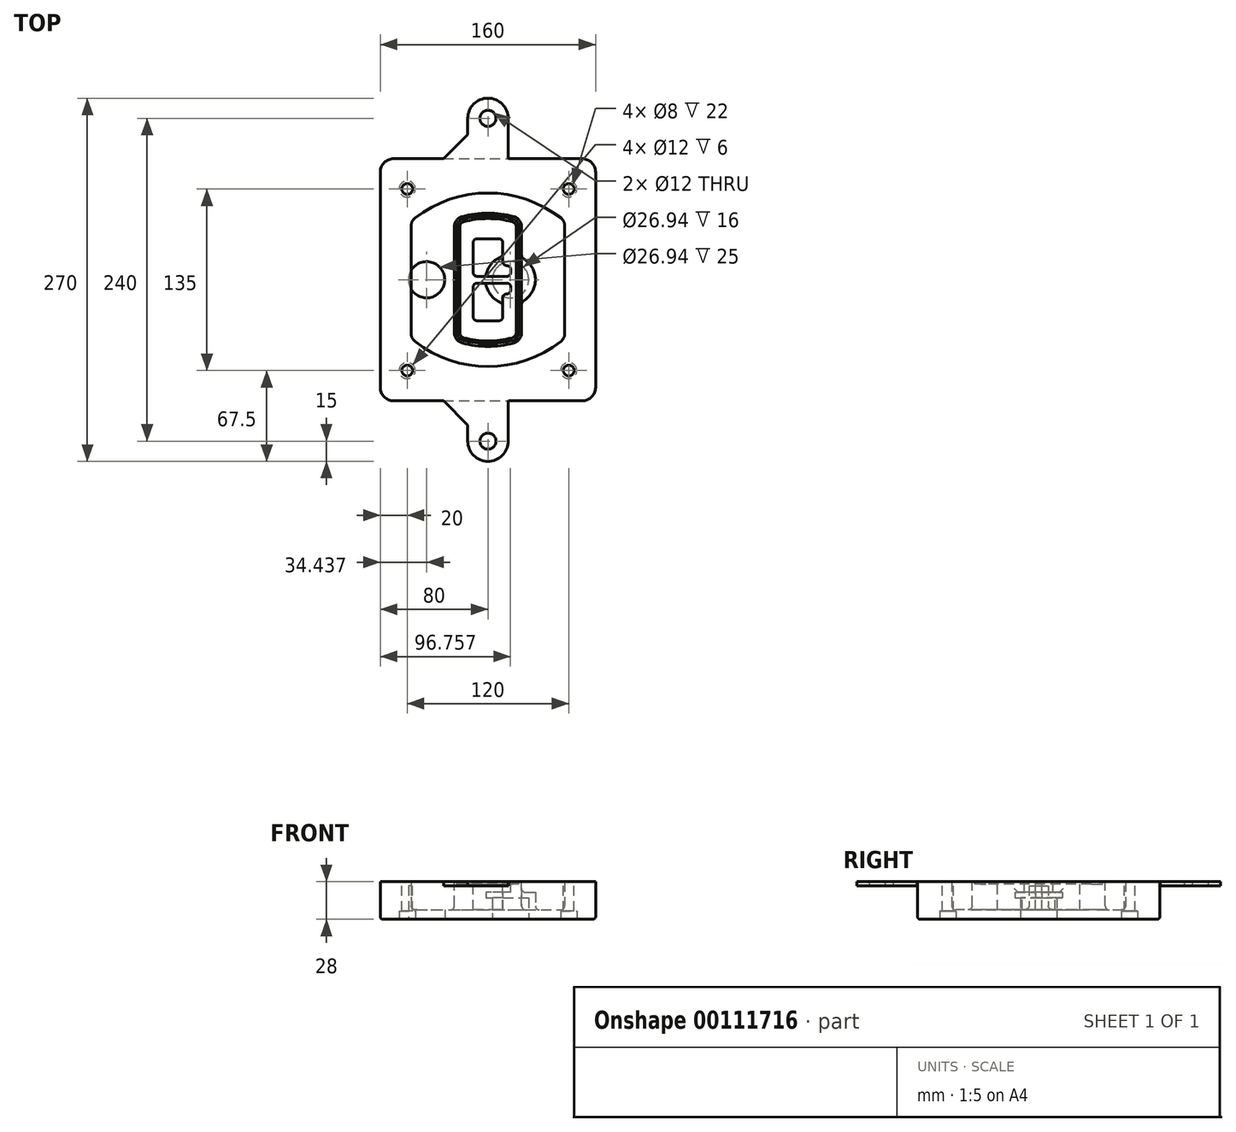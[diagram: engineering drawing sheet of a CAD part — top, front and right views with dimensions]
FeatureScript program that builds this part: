
annotation { "Feature Type Name" : "Feature", "Feature Type Description" : "" }
export const myFeature = defineFeature(function(context is Context, id is Id, definition is map)
    precondition{}
    {
        {
            var Q0;
            Q0=qCreatedBy(makeId("Top.planeOp"),FACE);
            var sketch = newSketch(context, id + "F0", { "sketchPlane" : qUnion([Q0])});
            skPoint(sketch, "E0.rect.middle", {"position": v(0, 0) * mm});
            skLineSegment(sketch, "E1.bottom", {"start": v(-70, -90) * mm, "end": v(70, -90) * mm});
            skLineSegment(sketch, "E1.top", {"start": v(-70, 90) * mm, "end": v(70, 90) * mm});
            skLineSegment(sketch, "E1.left", {"start": v(-80, -80) * mm, "end": v(-80, 80) * mm});
            skLineSegment(sketch, "E1.right", {"start": v(80, -80) * mm, "end": v(80, 80) * mm});
            skLineSegment(sketch, "E2", {"start": v(-80, 90) * mm, "end": v(80, -90) * mm, "construction": true});
            skLineSegment(sketch, "E3", {"start": v(80, 90) * mm, "end": v(-80, -90) * mm, "construction": true});
            skCircle(sketch, "E4", {"center": v(-60, 67.5) * mm, "radius": 4 * mm});
            skCircle(sketch, "E5", {"center": v(60, 67.5) * mm, "radius": 4 * mm});
            skCircle(sketch, "E6", {"center": v(60, -67.5) * mm, "radius": 4 * mm});
            skCircle(sketch, "E7", {"center": v(-60, -67.5) * mm, "radius": 4 * mm});
            skLineSegment(sketch, "E8", {"start": v(-60, 67.5) * mm, "end": v(60, 67.5) * mm, "construction": true});
            skLineSegment(sketch, "E9", {"start": v(60, 67.5) * mm, "end": v(60, -67.5) * mm, "construction": true});
            skLineSegment(sketch, "E10", {"start": v(60, -67.5) * mm, "end": v(-60, -67.5) * mm, "construction": true});
            skLineSegment(sketch, "E11", {"start": v(-60, -67.5) * mm, "end": v(-60, 67.5) * mm, "construction": true});
            skLineSegment(sketch, "E12", {"start": v(-60, 40.3) * mm, "end": v(-60, -40.3) * mm});
            skLineSegment(sketch, "E13", {"start": v(60, 40.3) * mm, "end": v(60, -40.3) * mm});
            skArc(sketch, "E14", {"start": v(56.15, 48.18) * mm, "mid": v(0, 67.5) * mm, "end": v(-56.15, 48.18) * mm});
            skArc(sketch, "E15", {"start": v(-56.15, -48.18) * mm, "mid": v(0, -67.5) * mm, "end": v(56.15, -48.18) * mm});
            skLineSegment(sketch, "E16", {"start": v(-60, 0) * mm, "end": v(60, 0) * mm, "construction": true});
            skPoint(sketch, "E17.visualSharp", {"position": v(-60, -45) * mm});
            skArc(sketch, "E17.filletArc", {"start": v(-60, -40.3) * mm, "mid": v(-58.99, -44.68) * mm, "end": v(-56.15, -48.18) * mm});
            skPoint(sketch, "E18.visualSharp", {"position": v(-60, 45) * mm});
            skArc(sketch, "E18.filletArc", {"start": v(-56.15, 48.18) * mm, "mid": v(-58.99, 44.68) * mm, "end": v(-60, 40.3) * mm});
            skPoint(sketch, "E19.visualSharp", {"position": v(60, 45) * mm});
            skArc(sketch, "E19.filletArc", {"start": v(60, 40.3) * mm, "mid": v(58.99, 44.68) * mm, "end": v(56.15, 48.18) * mm});
            skPoint(sketch, "E20.visualSharp", {"position": v(60, -45) * mm});
            skArc(sketch, "E20.filletArc", {"start": v(56.15, -48.18) * mm, "mid": v(58.99, -44.68) * mm, "end": v(60, -40.3) * mm});
            skPoint(sketch, "E21.visualSharp", {"position": v(-80, 90) * mm});
            skArc(sketch, "E21.filletArc", {"start": v(-70, 90) * mm, "mid": v(-77.07, 87.07) * mm, "end": v(-80, 80) * mm});
            skPoint(sketch, "E22.visualSharp", {"position": v(80, 90) * mm});
            skArc(sketch, "E22.filletArc", {"start": v(80, 80) * mm, "mid": v(77.07, 87.07) * mm, "end": v(70, 90) * mm});
            skPoint(sketch, "E23.visualSharp", {"position": v(80, -90) * mm});
            skArc(sketch, "E23.filletArc", {"start": v(70, -90) * mm, "mid": v(77.07, -87.07) * mm, "end": v(80, -80) * mm});
            skPoint(sketch, "E24.visualSharp", {"position": v(-80, -90) * mm});
            skArc(sketch, "E24.filletArc", {"start": v(-80, -80) * mm, "mid": v(-77.07, -87.07) * mm, "end": v(-70, -90) * mm});
            skArc(sketch, "E25.0", {"start": v(57, 40.3) * mm, "mid": v(56.3, 43.36) * mm, "end": v(54.3, 45.81) * mm});
            skLineSegment(sketch, "E25.1", {"start": v(57, 40.3) * mm, "end": v(57, -40.3) * mm});
            skArc(sketch, "E25.2", {"start": v(54.3, -45.81) * mm, "mid": v(56.3, -43.36) * mm, "end": v(57, -40.3) * mm});
            skArc(sketch, "E25.3", {"start": v(-54.3, -45.81) * mm, "mid": v(0, -64.5) * mm, "end": v(54.3, -45.81) * mm});
            skArc(sketch, "E25.4", {"start": v(-57, -40.3) * mm, "mid": v(-56.3, -43.36) * mm, "end": v(-54.3, -45.81) * mm});
            skArc(sketch, "E25.5", {"start": v(54.3, 45.81) * mm, "mid": v(0, 64.5) * mm, "end": v(-54.3, 45.81) * mm});
            skLineSegment(sketch, "E25.6", {"start": v(-57, 40.3) * mm, "end": v(-57, -40.3) * mm});
            skArc(sketch, "E25.7", {"start": v(-54.3, 45.81) * mm, "mid": v(-56.3, 43.36) * mm, "end": v(-57, 40.3) * mm});
            skArc(sketch, "E26.0", {"start": v(-58.62, 51.33) * mm, "mid": v(-62.58, 46.43) * mm, "end": v(-64, 40.3) * mm});
            skArc(sketch, "E26.1", {"start": v(58.62, 51.33) * mm, "mid": v(0, 71.5) * mm, "end": v(-58.62, 51.33) * mm});
            skArc(sketch, "E26.2", {"start": v(64, 40.3) * mm, "mid": v(62.58, 46.43) * mm, "end": v(58.62, 51.33) * mm});
            skLineSegment(sketch, "E26.3", {"start": v(64, 40.3) * mm, "end": v(64, -40.3) * mm});
            skArc(sketch, "E26.4", {"start": v(58.62, -51.33) * mm, "mid": v(62.58, -46.43) * mm, "end": v(64, -40.3) * mm});
            skLineSegment(sketch, "E26.5", {"start": v(-64, 40.3) * mm, "end": v(-64, -40.3) * mm});
            skArc(sketch, "E26.6", {"start": v(-58.62, -51.33) * mm, "mid": v(0, -71.5) * mm, "end": v(58.62, -51.33) * mm});
            skArc(sketch, "E26.7", {"start": v(-64, -40.3) * mm, "mid": v(-62.58, -46.43) * mm, "end": v(-58.62, -51.33) * mm});
            skSolve(sketch);
        }
        {
            var Q0;
            Q0=makeQuery(id+"F0.imprint","IMPRINT",FACE,{"disambiguationData":[TD([[makeQuery(id+"F0.imprint","IMPRINT",EDGE,{"derivedFrom":sQuery(id+"F0.wireOp",EDGE,"E1.bottom")}),1.0]])]});
            var Q1;
            Q1=makeQuery(id+"F0.imprint","IMPRINT",FACE,{"disambiguationData":[TD([[makeQuery(id+"F0.imprint","IMPRINT",EDGE,{"derivedFrom":sQuery(id+"F0.wireOp",EDGE,"E12")}),1.0]])]});
            var Q2;
            Q2=makeQuery(id+"F0.imprint","IMPRINT",FACE,{"disambiguationData":[TD([[makeQuery(id+"F0.imprint","IMPRINT",EDGE,{"derivedFrom":sQuery(id+"F0.wireOp",EDGE,"E25.0")}),1.0]])]});
            var Q3;
            Q3=makeQuery(id+"F0.imprint","IMPRINT",FACE,{"disambiguationData":[TD([[makeQuery(id+"F0.imprint","IMPRINT",EDGE,{"derivedFrom":sQuery(id+"F0.wireOp",EDGE,"E12")}),-1.0]])]});
            extrude(context, id + "F1", {"entities" : qUnion([Q0, Q1, Q2, Q3]), "oppositeDirection" : true, "depth" : 25 * mm});
        }
        {
            var Q0;
            Q0=makeQuery(id+"F0.imprint","IMPRINT",FACE,{"disambiguationData":[TD([[makeQuery(id+"F0.imprint","IMPRINT",EDGE,{"derivedFrom":sQuery(id+"F0.wireOp",EDGE,"E12")}),1.0]])]});
            extrude(context, id + "F2", {"entities" : qUnion([Q0]), "operationType" : NewBodyOperationType.ADD, "depth" : 3 * mm});
        }
        {
            var Q0;
            Q0=makeQuery(id+"F0.imprint","IMPRINT",FACE,{"disambiguationData":[TD([[makeQuery(id+"F0.imprint","IMPRINT",EDGE,{"derivedFrom":sQuery(id+"F0.wireOp",EDGE,"E25.0")}),1.0]])]});
            extrude(context, id + "F3", {"entities" : qUnion([Q0]), "operationType" : NewBodyOperationType.REMOVE, "oppositeDirection" : true, "depth" : 18 * mm});
        }
        {
            var Q0;
            Q0=makeQuery(id+"F2.opExtrude","CAP_FACE",FACE,{"disambiguationData":[OSD([sQuery(id+"F0.wireOp",EDGE,"E12"),sQuery(id+"F0.wireOp",EDGE,"E13"),sQuery(id+"F0.wireOp",EDGE,"E14"),sQuery(id+"F0.wireOp",EDGE,"E15"),sQuery(id+"F0.wireOp",EDGE,"E17.filletArc"),sQuery(id+"F0.wireOp",EDGE,"E18.filletArc"),sQuery(id+"F0.wireOp",EDGE,"E19.filletArc"),sQuery(id+"F0.wireOp",EDGE,"E20.filletArc"),sQuery(id+"F0.wireOp",EDGE,"E25.0"),sQuery(id+"F0.wireOp",EDGE,"E25.1"),sQuery(id+"F0.wireOp",EDGE,"E25.2"),sQuery(id+"F0.wireOp",EDGE,"E25.3"),sQuery(id+"F0.wireOp",EDGE,"E25.4"),sQuery(id+"F0.wireOp",EDGE,"E25.5"),sQuery(id+"F0.wireOp",EDGE,"E25.6"),sQuery(id+"F0.wireOp",EDGE,"E25.7")])],"isStart":false});
            var sketch = newSketch(context, id + "F4", { "sketchPlane" : qUnion([Q0])});
            skArc(sketch, "E27.0", {"start": v(-19.08, -46.97) * mm, "mid": v(0, -49.5) * mm, "end": v(19.08, -46.97) * mm});
            skArc(sketch, "E28.0", {"start": v(19.08, 46.97) * mm, "mid": v(0, 49.5) * mm, "end": v(-19.08, 46.97) * mm});
            skLineSegment(sketch, "E29", {"start": v(-25, 39.25) * mm, "end": v(-25, -39.25) * mm});
            skLineSegment(sketch, "E30", {"start": v(25, 39.25) * mm, "end": v(25, -39.25) * mm});
            skLineSegment(sketch, "E31", {"start": v(-25, 45.1) * mm, "end": v(25, 45.1) * mm, "construction": true});
            skLineSegment(sketch, "E32", {"start": v(-25, -45.1) * mm, "end": v(25, -45.1) * mm, "construction": true});
            skPoint(sketch, "E33.visualSharp", {"position": v(-25, 45.1) * mm});
            skArc(sketch, "E33.filletArc", {"start": v(-19.08, 46.97) * mm, "mid": v(-23.35, 44.11) * mm, "end": v(-25, 39.25) * mm});
            skPoint(sketch, "E34.visualSharp", {"position": v(25, 45.1) * mm});
            skArc(sketch, "E34.filletArc", {"start": v(25, 39.25) * mm, "mid": v(23.35, 44.11) * mm, "end": v(19.08, 46.97) * mm});
            skPoint(sketch, "E35.visualSharp", {"position": v(25, -45.1) * mm});
            skArc(sketch, "E35.filletArc", {"start": v(19.08, -46.97) * mm, "mid": v(23.35, -44.11) * mm, "end": v(25, -39.25) * mm});
            skPoint(sketch, "E36.visualSharp", {"position": v(-25, -45.1) * mm});
            skArc(sketch, "E36.filletArc", {"start": v(-25, -39.25) * mm, "mid": v(-23.35, -44.11) * mm, "end": v(-19.08, -46.97) * mm});
            skArc(sketch, "E37.0", {"start": v(54.3, 45.81) * mm, "mid": v(0, 64.5) * mm, "end": v(-54.3, 45.81) * mm});
            skArc(sketch, "E37.1", {"start": v(-54.3, 45.81) * mm, "mid": v(-56.3, 43.36) * mm, "end": v(-57, 40.3) * mm});
            skLineSegment(sketch, "E37.2", {"start": v(-57, 40.3) * mm, "end": v(-57, -40.3) * mm});
            skArc(sketch, "E37.3", {"start": v(-57, -40.3) * mm, "mid": v(-56.3, -43.36) * mm, "end": v(-54.3, -45.81) * mm});
            skArc(sketch, "E37.4", {"start": v(-54.3, -45.81) * mm, "mid": v(0, -64.5) * mm, "end": v(54.3, -45.81) * mm});
            skArc(sketch, "E37.5", {"start": v(54.3, -45.81) * mm, "mid": v(56.3, -43.36) * mm, "end": v(57, -40.3) * mm});
            skLineSegment(sketch, "E37.6", {"start": v(57, 40.3) * mm, "end": v(57, -40.3) * mm});
            skArc(sketch, "E37.7", {"start": v(57, 40.3) * mm, "mid": v(56.3, 43.36) * mm, "end": v(54.3, 45.81) * mm});
            skLineSegment(sketch, "E38.0", {"start": v(23, 39.25) * mm, "end": v(23, -39.25) * mm});
            skArc(sketch, "E38.1", {"start": v(18.56, -45.04) * mm, "mid": v(21.76, -42.9) * mm, "end": v(23, -39.25) * mm});
            skArc(sketch, "E38.2", {"start": v(-18.56, -45.04) * mm, "mid": v(0, -47.5) * mm, "end": v(18.56, -45.04) * mm});
            skArc(sketch, "E38.3", {"start": v(-23, -39.25) * mm, "mid": v(-21.76, -42.9) * mm, "end": v(-18.56, -45.04) * mm});
            skLineSegment(sketch, "E38.4", {"start": v(-23, 39.25) * mm, "end": v(-23, -39.25) * mm});
            skArc(sketch, "E38.5", {"start": v(23, 39.25) * mm, "mid": v(21.76, 42.9) * mm, "end": v(18.56, 45.04) * mm});
            skArc(sketch, "E38.6", {"start": v(-18.56, 45.04) * mm, "mid": v(-21.76, 42.9) * mm, "end": v(-23, 39.25) * mm});
            skArc(sketch, "E38.7", {"start": v(18.56, 45.04) * mm, "mid": v(0, 47.5) * mm, "end": v(-18.56, 45.04) * mm});
            skArc(sketch, "E39.0", {"start": v(21, 39.25) * mm, "mid": v(20.18, 41.68) * mm, "end": v(18.04, 43.1) * mm});
            skLineSegment(sketch, "E39.1", {"start": v(21, 39.25) * mm, "end": v(21, -39.25) * mm});
            skArc(sketch, "E39.2", {"start": v(18.04, -43.1) * mm, "mid": v(20.18, -41.68) * mm, "end": v(21, -39.25) * mm});
            skArc(sketch, "E39.3", {"start": v(-18.04, -43.1) * mm, "mid": v(0, -45.5) * mm, "end": v(18.04, -43.1) * mm});
            skArc(sketch, "E39.4", {"start": v(-21, -39.25) * mm, "mid": v(-20.18, -41.68) * mm, "end": v(-18.04, -43.1) * mm});
            skArc(sketch, "E39.5", {"start": v(18.04, 43.1) * mm, "mid": v(0, 45.5) * mm, "end": v(-18.04, 43.1) * mm});
            skLineSegment(sketch, "E39.6", {"start": v(-21, 39.25) * mm, "end": v(-21, -39.25) * mm});
            skArc(sketch, "E39.7", {"start": v(-18.04, 43.1) * mm, "mid": v(-20.18, 41.68) * mm, "end": v(-21, 39.25) * mm});
            skLineSegment(sketch, "E40", {"start": v(-25, 0) * mm, "end": v(25, 0) * mm, "construction": true});
            skLineSegment(sketch, "E41", {"start": v(-11, 5.5) * mm, "end": v(-11, 27.5) * mm});
            skLineSegment(sketch, "E42", {"start": v(-8, 30.5) * mm, "end": v(8, 30.5) * mm});
            skLineSegment(sketch, "E43", {"start": v(11, 27.5) * mm, "end": v(11, 13.5) * mm});
            skLineSegment(sketch, "E44", {"start": v(14, 10.5) * mm, "end": v(14, 10.5) * mm});
            skLineSegment(sketch, "E45", {"start": v(17, 7.5) * mm, "end": v(17, 5.5) * mm});
            skLineSegment(sketch, "E46", {"start": v(14, 2.5) * mm, "end": v(-8, 2.5) * mm});
            skPoint(sketch, "E47.visualSharp", {"position": v(-11, 30.5) * mm});
            skArc(sketch, "E47.filletArc", {"start": v(-8, 30.5) * mm, "mid": v(-10.12, 29.62) * mm, "end": v(-11, 27.5) * mm});
            skPoint(sketch, "E48.visualSharp", {"position": v(11, 30.5) * mm});
            skArc(sketch, "E48.filletArc", {"start": v(11, 27.5) * mm, "mid": v(10.12, 29.62) * mm, "end": v(8, 30.5) * mm});
            skPoint(sketch, "E49.visualSharp", {"position": v(11, 10.5) * mm});
            skArc(sketch, "E49.filletArc", {"start": v(11, 13.5) * mm, "mid": v(11.88, 11.38) * mm, "end": v(14, 10.5) * mm});
            skPoint(sketch, "E50.visualSharp", {"position": v(17, 10.5) * mm});
            skArc(sketch, "E50.filletArc", {"start": v(17, 7.5) * mm, "mid": v(16.12, 9.62) * mm, "end": v(14, 10.5) * mm});
            skPoint(sketch, "E51.visualSharp", {"position": v(17, 2.5) * mm});
            skArc(sketch, "E51.filletArc", {"start": v(14, 2.5) * mm, "mid": v(16.12, 3.38) * mm, "end": v(17, 5.5) * mm});
            skPoint(sketch, "E52.visualSharp", {"position": v(-11, 2.5) * mm});
            skArc(sketch, "E52.filletArc", {"start": v(-11, 5.5) * mm, "mid": v(-10.12, 3.38) * mm, "end": v(-8, 2.5) * mm});
            skLineSegment(sketch, "E53.0.MirrorCS", {"start": v(14, -2.5) * mm, "end": v(-8, -2.5) * mm});
            skArc(sketch, "E54.0.MirrorCS", {"start": v(-11, -5.5) * mm, "mid": v(-10.12, -3.38) * mm, "end": v(-8, -2.5) * mm});
            skLineSegment(sketch, "E55.0.MirrorCS", {"start": v(-11, -5.5) * mm, "end": v(-11, -27.5) * mm});
            skArc(sketch, "E56.0.MirrorCS", {"start": v(-8, -30.5) * mm, "mid": v(-10.12, -29.62) * mm, "end": v(-11, -27.5) * mm});
            skLineSegment(sketch, "E57.0.MirrorCS", {"start": v(-8, -30.5) * mm, "end": v(8, -30.5) * mm});
            skArc(sketch, "E58.0.MirrorCS", {"start": v(11, -27.5) * mm, "mid": v(10.12, -29.62) * mm, "end": v(8, -30.5) * mm});
            skLineSegment(sketch, "E59.0.MirrorCS", {"start": v(11, -27.5) * mm, "end": v(11, -13.5) * mm});
            skArc(sketch, "E60.0.MirrorCS", {"start": v(11, -13.5) * mm, "mid": v(11.88, -11.38) * mm, "end": v(14, -10.5) * mm});
            skArc(sketch, "E61.0.MirrorCS", {"start": v(17, -7.5) * mm, "mid": v(16.12, -9.62) * mm, "end": v(14, -10.5) * mm});
            skLineSegment(sketch, "E62.0.MirrorCS", {"start": v(17, -7.5) * mm, "end": v(17, -5.5) * mm});
            skArc(sketch, "E63.0.MirrorCS", {"start": v(14, -2.5) * mm, "mid": v(16.12, -3.38) * mm, "end": v(17, -5.5) * mm});
            skSolve(sketch);
        }
        {
            var Q0;
            Q0=makeQuery(id+"F4.imprint","IMPRINT",FACE,{"disambiguationData":[TD([[makeQuery(id+"F4.imprint","IMPRINT",EDGE,{"derivedFrom":sQuery(id+"F4.wireOp",EDGE,"E27.0")}),1.0]])]});
            var Q1;
            Q1=makeQuery(id+"F4.imprint","IMPRINT",FACE,{"disambiguationData":[TD([[makeQuery(id+"F4.imprint","IMPRINT",EDGE,{"derivedFrom":sQuery(id+"F4.wireOp",EDGE,"E38.0")}),-1.0]])]});
            var Q2;
            Q2=makeQuery(id+"F4.imprint","IMPRINT",FACE,{"disambiguationData":[TD([[makeQuery(id+"F4.imprint","IMPRINT",EDGE,{"derivedFrom":sQuery(id+"F4.wireOp",EDGE,"E39.0")}),1.0]])]});
            extrude(context, id + "F5", {"entities" : qUnion([Q0, Q1, Q2]), "operationType" : NewBodyOperationType.ADD, "endBound" : BoundingType.UP_TO_NEXT, "oppositeDirection" : true, "depth" : 25 * mm});
        }
        {
            var Q0;
            Q0=makeQuery(id+"F4.imprint","IMPRINT",FACE,{"disambiguationData":[TD([[makeQuery(id+"F4.imprint","IMPRINT",EDGE,{"derivedFrom":sQuery(id+"F4.wireOp",EDGE,"E38.0")}),-1.0]])]});
            extrude(context, id + "F6", {"entities" : qUnion([Q0]), "operationType" : NewBodyOperationType.REMOVE, "oppositeDirection" : true, "depth" : 2 * mm});
        }
        {
            var Q0;
            Q0=makeQuery(id+"F1.opExtrude","CAP_FACE",FACE,{"disambiguationData":[OSD([sQuery(id+"F0.wireOp",EDGE,"E1.bottom"),sQuery(id+"F0.wireOp",EDGE,"E1.top"),sQuery(id+"F0.wireOp",EDGE,"E1.left"),sQuery(id+"F0.wireOp",EDGE,"E1.right"),sQuery(id+"F0.wireOp",EDGE,"E4"),sQuery(id+"F0.wireOp",EDGE,"E5"),sQuery(id+"F0.wireOp",EDGE,"E6"),sQuery(id+"F0.wireOp",EDGE,"E7"),sQuery(id+"F0.wireOp",EDGE,"E21.filletArc"),sQuery(id+"F0.wireOp",EDGE,"E22.filletArc"),sQuery(id+"F0.wireOp",EDGE,"E23.filletArc"),sQuery(id+"F0.wireOp",EDGE,"E24.filletArc")])],"isStart":false});
            var sketch = newSketch(context, id + "F7", { "sketchPlane" : qUnion([Q0])});
            skCircle(sketch, "E64", {"center": v(16.76, 0) * mm, "radius": 13.47 * mm});
            skCircle(sketch, "E65", {"center": v(-45.56, 0) * mm, "radius": 13.47 * mm});
            skLineSegment(sketch, "E66", {"start": v(80, 0) * mm, "end": v(-80, 0) * mm});
            skCircle(sketch, "E67", {"center": v(16.76, 0) * mm, "radius": 18.47 * mm});
            skCircle(sketch, "E68", {"center": v(60, -67.5) * mm, "radius": 6 * mm});
            skCircle(sketch, "E69", {"center": v(-60, -67.5) * mm, "radius": 6 * mm});
            skCircle(sketch, "E70", {"center": v(-60, 67.5) * mm, "radius": 6 * mm});
            skCircle(sketch, "E71", {"center": v(60, 67.5) * mm, "radius": 6 * mm});
            skSolve(sketch);
        }
        {
            var Q0;
            {var subQ1=sQuery(id+"F7.wireOp",EDGE,"E66");var subQ4=sQuery(id+"F7.wireOp",EDGE,"E64");var subQ6=makeQuery(id+"F7.imprint","INTERSECT",VERTEX,{"disambiguationData":[OD(0.0)],"derivedFrom":[subQ4,subQ1]});Q0=makeQuery(id+"F7.imprint","IMPRINT",FACE,{"disambiguationData":[TD([[makeQuery(id+"F7.imprint","IMPRINT",EDGE,{"disambiguationData":[TD([[subQ6,-1.0]])],"derivedFrom":subQ4}),-1.0]])]});}
            var Q1;
            {var subQ0=sQuery(id+"F7.wireOp",EDGE,"E66");var subQ1=sQuery(id+"F7.wireOp",EDGE,"E64");var subQ3=makeQuery(id+"F7.imprint","INTERSECT",VERTEX,{"disambiguationData":[OD(0.0)],"derivedFrom":[subQ1,subQ0]});Q1=makeQuery(id+"F7.imprint","IMPRINT",FACE,{"disambiguationData":[TD([[makeQuery(id+"F7.imprint","IMPRINT",EDGE,{"disambiguationData":[TD([[subQ3,-1.0]])],"derivedFrom":subQ1}),1.0]])]});}
            var Q2;
            {var subQ0=sQuery(id+"F7.wireOp",EDGE,"E66");var subQ1=sQuery(id+"F7.wireOp",EDGE,"E64");var subQ3=makeQuery(id+"F7.imprint","INTERSECT",VERTEX,{"disambiguationData":[OD(0.0)],"derivedFrom":[subQ1,subQ0]});Q2=makeQuery(id+"F7.imprint","IMPRINT",FACE,{"disambiguationData":[TD([[makeQuery(id+"F7.imprint","IMPRINT",EDGE,{"disambiguationData":[TD([[subQ3,1.0]])],"derivedFrom":subQ1}),1.0]])]});}
            var Q3;
            {var subQ1=sQuery(id+"F7.wireOp",EDGE,"E66");var subQ4=sQuery(id+"F7.wireOp",EDGE,"E64");var subQ6=makeQuery(id+"F7.imprint","INTERSECT",VERTEX,{"disambiguationData":[OD(0.0)],"derivedFrom":[subQ4,subQ1]});Q3=makeQuery(id+"F7.imprint","IMPRINT",FACE,{"disambiguationData":[TD([[makeQuery(id+"F7.imprint","IMPRINT",EDGE,{"disambiguationData":[TD([[subQ6,1.0]])],"derivedFrom":subQ4}),-1.0]])]});}
            extrude(context, id + "F8", {"entities" : qUnion([Q0, Q1, Q2, Q3]), "operationType" : NewBodyOperationType.ADD, "oppositeDirection" : true, "depth" : 20 * mm});
        }
        {
            var Q0;
            {var subQ0=sQuery(id+"F7.wireOp",EDGE,"E66");var subQ1=sQuery(id+"F7.wireOp",EDGE,"E64");var subQ3=makeQuery(id+"F7.imprint","INTERSECT",VERTEX,{"disambiguationData":[OD(0.0)],"derivedFrom":[subQ1,subQ0]});Q0=makeQuery(id+"F7.imprint","IMPRINT",FACE,{"disambiguationData":[TD([[makeQuery(id+"F7.imprint","IMPRINT",EDGE,{"disambiguationData":[TD([[subQ3,-1.0]])],"derivedFrom":subQ1}),1.0]])]});}
            var Q1;
            {var subQ0=sQuery(id+"F7.wireOp",EDGE,"E66");var subQ1=sQuery(id+"F7.wireOp",EDGE,"E64");var subQ3=makeQuery(id+"F7.imprint","INTERSECT",VERTEX,{"disambiguationData":[OD(0.0)],"derivedFrom":[subQ1,subQ0]});Q1=makeQuery(id+"F7.imprint","IMPRINT",FACE,{"disambiguationData":[TD([[makeQuery(id+"F7.imprint","IMPRINT",EDGE,{"disambiguationData":[TD([[subQ3,1.0]])],"derivedFrom":subQ1}),1.0]])]});}
            extrude(context, id + "F9", {"entities" : qUnion([Q0, Q1]), "operationType" : NewBodyOperationType.REMOVE, "oppositeDirection" : true, "depth" : 16 * mm});
        }
        {
            var Q0;
            {var subQ0=sQuery(id+"F7.wireOp",EDGE,"E66");var subQ1=sQuery(id+"F7.wireOp",EDGE,"E65");var subQ3=makeQuery(id+"F7.imprint","INTERSECT",VERTEX,{"disambiguationData":[OD(0.0)],"derivedFrom":[subQ1,subQ0]});Q0=makeQuery(id+"F7.imprint","IMPRINT",FACE,{"disambiguationData":[TD([[makeQuery(id+"F7.imprint","IMPRINT",EDGE,{"disambiguationData":[TD([[subQ3,-1.0]])],"derivedFrom":subQ1}),1.0]])]});}
            var Q1;
            {var subQ0=sQuery(id+"F7.wireOp",EDGE,"E66");var subQ1=sQuery(id+"F7.wireOp",EDGE,"E65");var subQ3=makeQuery(id+"F7.imprint","INTERSECT",VERTEX,{"disambiguationData":[OD(0.0)],"derivedFrom":[subQ1,subQ0]});Q1=makeQuery(id+"F7.imprint","IMPRINT",FACE,{"disambiguationData":[TD([[makeQuery(id+"F7.imprint","IMPRINT",EDGE,{"disambiguationData":[TD([[subQ3,1.0]])],"derivedFrom":subQ1}),1.0]])]});}
            extrude(context, id + "F10", {"entities" : qUnion([Q0, Q1]), "operationType" : NewBodyOperationType.REMOVE, "oppositeDirection" : true, "depth" : 25 * mm});
        }
        {
            var Q0;
            Q0=makeQuery(id+"F7.imprint","IMPRINT",FACE,{"disambiguationData":[TD([[makeQuery(id+"F7.imprint","IMPRINT",EDGE,{"derivedFrom":sQuery(id+"F7.wireOp",EDGE,"E68")}),1.0]])]});
            var Q1;
            Q1=makeQuery(id+"F7.imprint","IMPRINT",FACE,{"disambiguationData":[TD([[makeQuery(id+"F7.imprint","IMPRINT",EDGE,{"derivedFrom":makeQuery(id+"F1.opExtrude","CAP_EDGE",EDGE,{"disambiguationData":[OSD([sQuery(id+"F0.wireOp",EDGE,"E5")])],"isStart":false})}),-1.0]])]});
            var Q2;
            Q2=makeQuery(id+"F7.imprint","IMPRINT",FACE,{"disambiguationData":[TD([[makeQuery(id+"F7.imprint","IMPRINT",EDGE,{"derivedFrom":sQuery(id+"F7.wireOp",EDGE,"E69")}),1.0]])]});
            var Q3;
            Q3=makeQuery(id+"F7.imprint","IMPRINT",FACE,{"disambiguationData":[TD([[makeQuery(id+"F7.imprint","IMPRINT",EDGE,{"derivedFrom":makeQuery(id+"F1.opExtrude","CAP_EDGE",EDGE,{"disambiguationData":[OSD([sQuery(id+"F0.wireOp",EDGE,"E4")])],"isStart":false})}),-1.0]])]});
            var Q4;
            Q4=makeQuery(id+"F7.imprint","IMPRINT",FACE,{"disambiguationData":[TD([[makeQuery(id+"F7.imprint","IMPRINT",EDGE,{"derivedFrom":sQuery(id+"F7.wireOp",EDGE,"E70")}),1.0]])]});
            var Q5;
            Q5=makeQuery(id+"F7.imprint","IMPRINT",FACE,{"disambiguationData":[TD([[makeQuery(id+"F7.imprint","IMPRINT",EDGE,{"derivedFrom":makeQuery(id+"F1.opExtrude","CAP_EDGE",EDGE,{"disambiguationData":[OSD([sQuery(id+"F0.wireOp",EDGE,"E7")])],"isStart":false})}),-1.0]])]});
            var Q6;
            Q6=makeQuery(id+"F7.imprint","IMPRINT",FACE,{"disambiguationData":[TD([[makeQuery(id+"F7.imprint","IMPRINT",EDGE,{"derivedFrom":sQuery(id+"F7.wireOp",EDGE,"E71")}),1.0]])]});
            var Q7;
            Q7=makeQuery(id+"F7.imprint","IMPRINT",FACE,{"disambiguationData":[TD([[makeQuery(id+"F7.imprint","IMPRINT",EDGE,{"derivedFrom":makeQuery(id+"F1.opExtrude","CAP_EDGE",EDGE,{"disambiguationData":[OSD([sQuery(id+"F0.wireOp",EDGE,"E6")])],"isStart":false})}),-1.0]])]});
            extrude(context, id + "F11", {"entities" : qUnion([Q0, Q1, Q2, Q3, Q4, Q5, Q6, Q7]), "operationType" : NewBodyOperationType.REMOVE, "oppositeDirection" : true, "depth" : 6 * mm});
        }
        {
            var Q0;
            Q0=makeQuery(id+"F9.boolean.opBoolean","COPY",FACE,{"derivedFrom":makeQuery(id+"F9.opExtrude","CAP_FACE",FACE,{"disambiguationData":[OSD([sQuery(id+"F7.wireOp",EDGE,"E64")])],"isStart":false})});
            var sketch = newSketch(context, id + "F12", { "sketchPlane" : qUnion([Q0])});
            skArc(sketch, "E72.0", {"start": v(11, 17.55) * mm, "mid": v(2.57, 11.82) * mm, "end": v(-1.54, 2.5) * mm});
            skArc(sketch, "E72.1", {"start": v(-1.54, -2.5) * mm, "mid": v(2.57, -11.82) * mm, "end": v(11, -17.55) * mm});
            skLineSegment(sketch, "E73", {"start": v(-1.54, -2.5) * mm, "end": v(14, -2.5) * mm});
            skLineSegment(sketch, "E74.0", {"start": v(14, 2.5) * mm, "end": v(-1.54, 2.5) * mm});
            skArc(sketch, "E74.1", {"start": v(14, 2.5) * mm, "mid": v(16.12, 3.38) * mm, "end": v(17, 5.5) * mm});
            skLineSegment(sketch, "E74.2", {"start": v(17, 7.5) * mm, "end": v(17, 5.5) * mm});
            skArc(sketch, "E74.3", {"start": v(17, 7.5) * mm, "mid": v(16.12, 9.62) * mm, "end": v(14, 10.5) * mm});
            skArc(sketch, "E74.4", {"start": v(11, 13.5) * mm, "mid": v(11.88, 11.38) * mm, "end": v(14, 10.5) * mm});
            skLineSegment(sketch, "E74.5", {"start": v(11, 17.55) * mm, "end": v(11, 13.5) * mm});
            skLineSegment(sketch, "E74.7", {"start": v(14, -2.5) * mm, "end": v(-1.54, -2.5) * mm});
            skArc(sketch, "E74.8", {"start": v(14, -2.5) * mm, "mid": v(16.12, -3.38) * mm, "end": v(17, -5.5) * mm});
            skLineSegment(sketch, "E74.9", {"start": v(17, -7.5) * mm, "end": v(17, -5.5) * mm});
            skArc(sketch, "E74.10", {"start": v(17, -7.5) * mm, "mid": v(16.12, -9.62) * mm, "end": v(14, -10.5) * mm});
            skArc(sketch, "E74.11", {"start": v(11, -13.5) * mm, "mid": v(11.88, -11.38) * mm, "end": v(14, -10.5) * mm});
            skLineSegment(sketch, "E74.12", {"start": v(11, -17.55) * mm, "end": v(11, -13.5) * mm});
            skPoint(sketch, "E75.orphan", {"position": v(11, -27.5) * mm});
            skPoint(sketch, "E76.orphan", {"position": v(-8, -2.5) * mm});
            skPoint(sketch, "E77.orphan", {"position": v(-8, 2.5) * mm});
            skPoint(sketch, "E78.orphan", {"position": v(11, 27.5) * mm});
            skSolve(sketch);
        }
        {
            var Q0;
            {var subQ7=sQuery(id+"F12.wireOp",EDGE,"E72.0");var subQ14=sQuery(id+"F12.wireOp",EDGE,"E72.1");var subQ16=sQuery(id+"F12.wireOp",EDGE,"E74.1");var subQ18=sQuery(id+"F12.wireOp",EDGE,"E74.8");Q0=qUnion([makeQuery(id+"F12.imprint","IMPRINT",FACE,{"disambiguationData":[TD([[makeQuery(id+"F12.imprint","IMPRINT",EDGE,{"derivedFrom":subQ7}),1.0]])]}),makeQuery(id+"F12.imprint","IMPRINT",FACE,{"disambiguationData":[TD([[makeQuery(id+"F12.imprint","IMPRINT",EDGE,{"derivedFrom":subQ14}),1.0]])]}),makeQuery(id+"F12.imprint","IMPRINT",FACE,{"disambiguationData":[TD([[makeQuery(id+"F12.imprint","IMPRINT",EDGE,{"derivedFrom":subQ16}),1.0]])]}),makeQuery(id+"F12.imprint","IMPRINT",FACE,{"disambiguationData":[TD([[makeQuery(id+"F12.imprint","IMPRINT",EDGE,{"derivedFrom":subQ18}),-1.0]])]})]);}
            var Q1;
            Q1=makeQuery(id+"F5.boolean.opBoolean","SPLIT",FACE,{"disambiguationData":[TD([makeQuery(id+"F5.opExtrude","SWEPT_FACE",FACE,{"disambiguationData":[OSD([sQuery(id+"F4.wireOp",EDGE,"E41")])]})])],"derivedFrom":makeQuery(id+"F3.boolean.opBoolean","COPY",FACE,{"derivedFrom":makeQuery(id+"F3.opExtrude","CAP_FACE",FACE,{"disambiguationData":[OSD([sQuery(id+"F0.wireOp",EDGE,"E25.0"),sQuery(id+"F0.wireOp",EDGE,"E25.1"),sQuery(id+"F0.wireOp",EDGE,"E25.2"),sQuery(id+"F0.wireOp",EDGE,"E25.3"),sQuery(id+"F0.wireOp",EDGE,"E25.4"),sQuery(id+"F0.wireOp",EDGE,"E25.5"),sQuery(id+"F0.wireOp",EDGE,"E25.6"),sQuery(id+"F0.wireOp",EDGE,"E25.7")])],"isStart":false})})});
            extrude(context, id + "F13", {"entities" : qUnion([Q0]), "operationType" : NewBodyOperationType.REMOVE, "endBound" : BoundingType.UP_TO_SURFACE, "endBoundEntityFace" : qUnion([Q1]), "depth" : 25 * mm});
        }
        {
            var Q0;
            Q0=makeQuery(id+"F3.boolean.opBoolean","COPY",EDGE,{"derivedFrom":makeQuery(id+"F3.opExtrude","CAP_EDGE",EDGE,{"disambiguationData":[OSD([sQuery(id+"F0.wireOp",EDGE,"E25.6")])],"isStart":false})});
            var Q1;
            Q1=makeQuery(id+"F8.boolean.opBoolean","INTERSECT",EDGE,{"derivedFrom":[makeQuery(id+"F5.opExtrude","SWEPT_FACE",FACE,{"disambiguationData":[OSD([sQuery(id+"F4.wireOp",EDGE,"E30")])]}),makeQuery(id+"F8.opExtrude","CAP_FACE",FACE,{"disambiguationData":[OSD([sQuery(id+"F7.wireOp",EDGE,"E67")])],"isStart":false})]});
            var Q2;
            Q2=makeQuery(id+"F8.boolean.opBoolean","INTERSECT",EDGE,{"disambiguationData":[OD(1.0)],"derivedFrom":[makeQuery(id+"F5.opExtrude","SWEPT_FACE",FACE,{"disambiguationData":[OSD([sQuery(id+"F4.wireOp",EDGE,"E30")])]}),makeQuery(id+"F8.opExtrude","SWEPT_FACE",FACE,{"disambiguationData":[OSD([sQuery(id+"F7.wireOp",EDGE,"E67")])]})]});
            var Q3;
            {var subQ0=sQuery(id+"F4.wireOp",EDGE,"E30");Q3=makeQuery(id+"F8.boolean.opBoolean","SPLIT",EDGE,{"disambiguationData":[TD([makeQuery(id+"F5.opExtrude","SWEPT_FACE",FACE,{"disambiguationData":[OSD([sQuery(id+"F4.wireOp",EDGE,"E35.filletArc")])]})])],"derivedFrom":makeQuery(id+"F5.opExtrude","CAP_EDGE",EDGE,{"disambiguationData":[OSD([subQ0])],"isStart":false})});}
            var Q4;
            {var subQ0=sQuery(id+"F0.wireOp",EDGE,"E25.7");var subQ1=sQuery(id+"F0.wireOp",EDGE,"E25.1");var subQ2=sQuery(id+"F0.wireOp",EDGE,"E25.6");var subQ3=sQuery(id+"F0.wireOp",EDGE,"E25.5");var subQ4=sQuery(id+"F0.wireOp",EDGE,"E25.4");var subQ5=sQuery(id+"F0.wireOp",EDGE,"E25.0");var subQ6=sQuery(id+"F0.wireOp",EDGE,"E25.2");var subQ7=sQuery(id+"F0.wireOp",EDGE,"E25.3");Q4=makeQuery(id+"F8.boolean.opBoolean","INTERSECT",EDGE,{"derivedFrom":[makeQuery(id+"F5.boolean.opBoolean","SPLIT",FACE,{"disambiguationData":[TD([makeQuery(id+"F2.opExtrude","SWEPT_FACE",FACE,{"disambiguationData":[OSD([subQ5])]})])],"derivedFrom":makeQuery(id+"F3.boolean.opBoolean","COPY",FACE,{"derivedFrom":makeQuery(id+"F3.opExtrude","CAP_FACE",FACE,{"disambiguationData":[OSD([subQ5,subQ1,subQ6,subQ7,subQ4,subQ3,subQ2,subQ0])],"isStart":false})})}),makeQuery(id+"F8.opExtrude","SWEPT_FACE",FACE,{"disambiguationData":[OSD([sQuery(id+"F7.wireOp",EDGE,"E67")])]})]});}
            var Q5;
            Q5=makeQuery(id+"F8.boolean.opBoolean","INTERSECT",EDGE,{"disambiguationData":[OD(0.0)],"derivedFrom":[makeQuery(id+"F5.opExtrude","SWEPT_FACE",FACE,{"disambiguationData":[OSD([sQuery(id+"F4.wireOp",EDGE,"E30")])]}),makeQuery(id+"F8.opExtrude","SWEPT_FACE",FACE,{"disambiguationData":[OSD([sQuery(id+"F7.wireOp",EDGE,"E67")])]})]});
            fillet(context, id + "F14", {"entities" : qUnion([Q0, Q1, Q2, Q3, Q4, Q5]), "radius" : 3 * mm, "tangentPropagation" : true, "allowEdgeOverflow" : false});
        }
        {
            var Q0;
            Q0=makeQuery(id+"F1.opExtrude","CAP_EDGE",EDGE,{"disambiguationData":[OSD([sQuery(id+"F0.wireOp",EDGE,"E1.bottom")])],"isStart":false});
            fillet(context, id + "F15", {"entities" : qUnion([Q0]), "radius" : 2 * mm, "tangentPropagation" : true, "allowEdgeOverflow" : false});
        }
        {
            var Q0;
            {var subQ0=sQuery(id+"F0.wireOp",EDGE,"E22.filletArc");var subQ1=sQuery(id+"F0.wireOp",EDGE,"E7");var subQ2=sQuery(id+"F0.wireOp",EDGE,"E6");var subQ3=sQuery(id+"F0.wireOp",EDGE,"E5");var subQ4=sQuery(id+"F0.wireOp",EDGE,"E4");var subQ5=sQuery(id+"F0.wireOp",EDGE,"E1.bottom");var subQ6=sQuery(id+"F0.wireOp",EDGE,"E21.filletArc");var subQ7=sQuery(id+"F0.wireOp",EDGE,"E1.top");var subQ8=sQuery(id+"F0.wireOp",EDGE,"E1.left");var subQ9=sQuery(id+"F0.wireOp",EDGE,"E1.right");var subQ10=sQuery(id+"F0.wireOp",EDGE,"E23.filletArc");var subQ11=sQuery(id+"F0.wireOp",EDGE,"E24.filletArc");Q0=makeQuery(id+"F2.boolean.opBoolean","SPLIT",FACE,{"disambiguationData":[TD([makeQuery(id+"F1.opExtrude","SWEPT_FACE",FACE,{"disambiguationData":[OSD([subQ5])]})])],"derivedFrom":makeQuery(id+"F1.opExtrude","CAP_FACE",FACE,{"disambiguationData":[OSD([subQ5,subQ7,subQ8,subQ9,subQ4,subQ3,subQ2,subQ1,subQ6,subQ0,subQ10,subQ11])],"isStart":true})});}
            var sketch = newSketch(context, id + "F16", { "sketchPlane" : qUnion([Q0])});
            skLineSegment(sketch, "E79", {"start": v(0, 90) * mm, "end": v(0, 120) * mm, "construction": true});
            skPoint(sketch, "E79.endSnap0", {"position": v(0, 90) * mm});
            skLineSegment(sketch, "E80", {"start": v(15.3, 90) * mm, "end": v(15, 90.3) * mm});
            skLineSegment(sketch, "E81", {"start": v(-33, 90) * mm, "end": v(-15, 108) * mm});
            skLineSegment(sketch, "E82", {"start": v(-15, 108) * mm, "end": v(-15, 120) * mm});
            skLineSegment(sketch, "E83", {"start": v(15, 90.3) * mm, "end": v(15, 120) * mm});
            skArc(sketch, "E84", {"start": v(15, 120) * mm, "mid": v(0, 135) * mm, "end": v(-15, 120) * mm});
            skCircle(sketch, "E85", {"center": v(0, 120) * mm, "radius": 6 * mm});
            skLineSegment(sketch, "E86", {"start": v(-80, 0) * mm, "end": v(80, 0) * mm, "construction": true});
            skArc(sketch, "E87.MirrorCS", {"start": v(15, -120) * mm, "mid": v(0, -135) * mm, "end": v(-15, -120) * mm});
            skCircle(sketch, "E88.MirrorC", {"center": v(0, -120) * mm, "radius": 6 * mm});
            skLineSegment(sketch, "E89.MirrorCS", {"start": v(0, -90) * mm, "end": v(0, -120) * mm, "construction": true});
            skLineSegment(sketch, "E90.MirrorCS", {"start": v(-33, -90) * mm, "end": v(-15, -108) * mm});
            skLineSegment(sketch, "E91.MirrorCS", {"start": v(-15, -108) * mm, "end": v(-15, -120) * mm});
            skLineSegment(sketch, "E92.MirrorCS", {"start": v(15, -90.3) * mm, "end": v(15, -120) * mm});
            skLineSegment(sketch, "E93.MirrorCS", {"start": v(15.3, -90) * mm, "end": v(15, -90.3) * mm});
            skSolve(sketch);
        }
        {
            var Q0;
            {var subQ0=sQuery(id+"F16.wireOp",EDGE,"E90.MirrorCS");Q0=makeQuery(id+"F16.imprint","IMPRINT",FACE,{"disambiguationData":[TD([[makeQuery(id+"F16.imprint","IMPRINT",EDGE,{"derivedFrom":subQ0}),1.0]])]});}
            var Q1;
            Q1=makeQuery(id+"F16.imprint","IMPRINT",FACE,{"disambiguationData":[TD([[makeQuery(id+"F16.imprint","IMPRINT",EDGE,{"derivedFrom":makeQuery(id+"F1.opExtrude","CAP_EDGE",EDGE,{"disambiguationData":[OSD([sQuery(id+"F0.wireOp",EDGE,"E1.left")])],"isStart":true})}),-1.0]])]});
            var Q2;
            {var subQ0=sQuery(id+"F16.wireOp",EDGE,"E80");Q2=makeQuery(id+"F16.imprint","IMPRINT",FACE,{"disambiguationData":[TD([[makeQuery(id+"F16.imprint","IMPRINT",EDGE,{"derivedFrom":subQ0}),1.0]])]});}
            var Q3;
            Q3=makeQuery(id+"F2.opExtrude","CAP_FACE",FACE,{"disambiguationData":[OSD([sQuery(id+"F0.wireOp",EDGE,"E12"),sQuery(id+"F0.wireOp",EDGE,"E13"),sQuery(id+"F0.wireOp",EDGE,"E14"),sQuery(id+"F0.wireOp",EDGE,"E15"),sQuery(id+"F0.wireOp",EDGE,"E17.filletArc"),sQuery(id+"F0.wireOp",EDGE,"E18.filletArc"),sQuery(id+"F0.wireOp",EDGE,"E19.filletArc"),sQuery(id+"F0.wireOp",EDGE,"E20.filletArc"),sQuery(id+"F0.wireOp",EDGE,"E25.0"),sQuery(id+"F0.wireOp",EDGE,"E25.1"),sQuery(id+"F0.wireOp",EDGE,"E25.2"),sQuery(id+"F0.wireOp",EDGE,"E25.3"),sQuery(id+"F0.wireOp",EDGE,"E25.4"),sQuery(id+"F0.wireOp",EDGE,"E25.5"),sQuery(id+"F0.wireOp",EDGE,"E25.6"),sQuery(id+"F0.wireOp",EDGE,"E25.7")])],"isStart":false});
            extrude(context, id + "F17", {"entities" : qUnion([Q0, Q1, Q2]), "operationType" : NewBodyOperationType.ADD, "endBound" : BoundingType.UP_TO_SURFACE, "endBoundEntityFace" : qUnion([Q3]), "depth" : 25 * mm});
        }
    });
